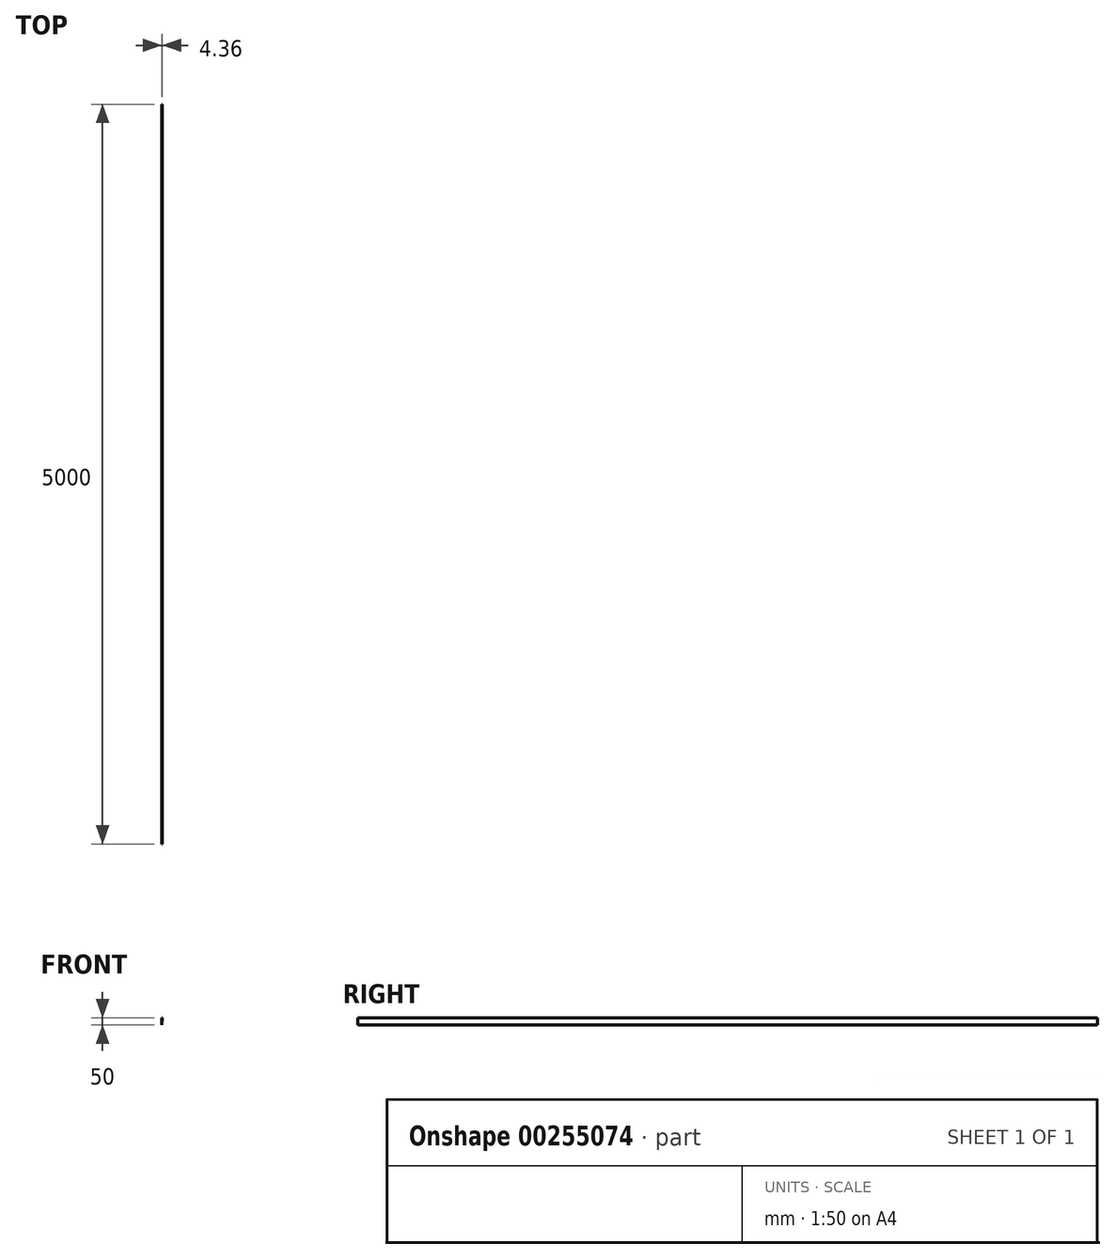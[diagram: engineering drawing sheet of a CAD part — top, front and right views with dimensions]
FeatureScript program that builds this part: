
annotation { "Feature Type Name" : "Feature", "Feature Type Description" : "" }
export const myFeature = defineFeature(function(context is Context, id is Id, definition is map)
    precondition{}
    {
        {
            var Q0;
            Q0=qCreatedBy(makeId("Front.planeOp"),FACE);
            var sketch = newSketch(context, id + "F0", { "sketchPlane" : qUnion([Q0])});
            skCircle(sketch, "E0", {"center": v(0, 0) * mm, "radius": 50 * mm});
            skLineSegment(sketch, "E1", {"start": v(0, 0) * mm, "end": v(0, 50) * mm});
            skLineSegment(sketch, "E2", {"start": v(0, 0) * mm, "end": v(4.36, 49.8) * mm});
            skSolve(sketch);
        }
        {
            var Q0;
            {var subQ0=sQuery(id+"F0.wireOp",EDGE,"E1");Q0=makeQuery(id+"F0.imprint","IMPRINT",FACE,{"disambiguationData":[TD([[makeQuery(id+"F0.imprint","IMPRINT",EDGE,{"derivedFrom":subQ0}),-1.0]])]});}
            extrude(context, id + "F1", {"entities" : qUnion([Q0]), "depth" : 5000 * mm});
        }
    });
